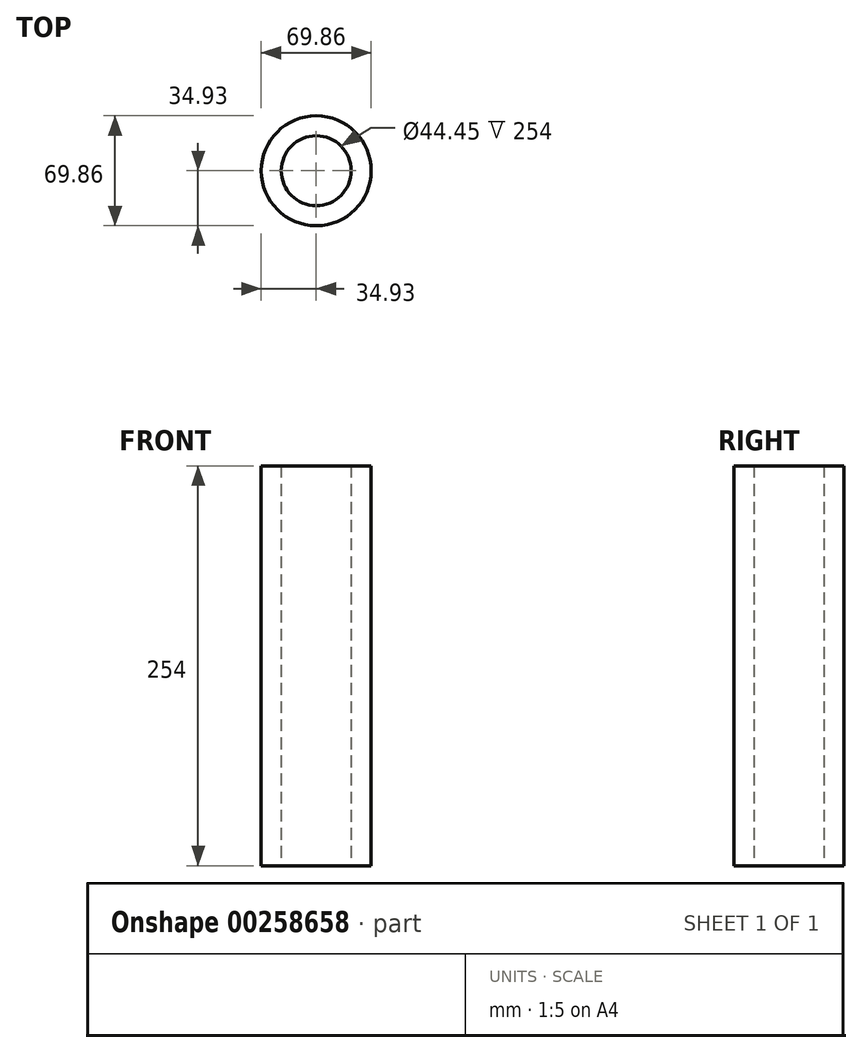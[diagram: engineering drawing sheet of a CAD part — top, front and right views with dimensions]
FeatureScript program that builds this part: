
annotation { "Feature Type Name" : "Feature", "Feature Type Description" : "" }
export const myFeature = defineFeature(function(context is Context, id is Id, definition is map)
    precondition{}
    {
        {
            var Q0;
            Q0=qCreatedBy(makeId("Top.planeOp"),FACE);
            var sketch = newSketch(context, id + "F0", { "sketchPlane" : qUnion([Q0])});
            skCircle(sketch, "E0", {"center": v(0, 0) * mm, "radius": 34.93 * mm});
            skCircle(sketch, "E1", {"center": v(0, 0) * mm, "radius": 22.23 * mm});
            skSolve(sketch);
        }
        {
            var Q0;
            Q0=makeQuery(id+"F0.imprint","IMPRINT",FACE,{"disambiguationData":[TD([[makeQuery(id+"F0.imprint","IMPRINT",EDGE,{"derivedFrom":sQuery(id+"F0.wireOp",EDGE,"E0")}),1.0]])]});
            extrude(context, id + "F1", {"entities" : qUnion([Q0]), "depth" : 254 * mm});
        }
    });
